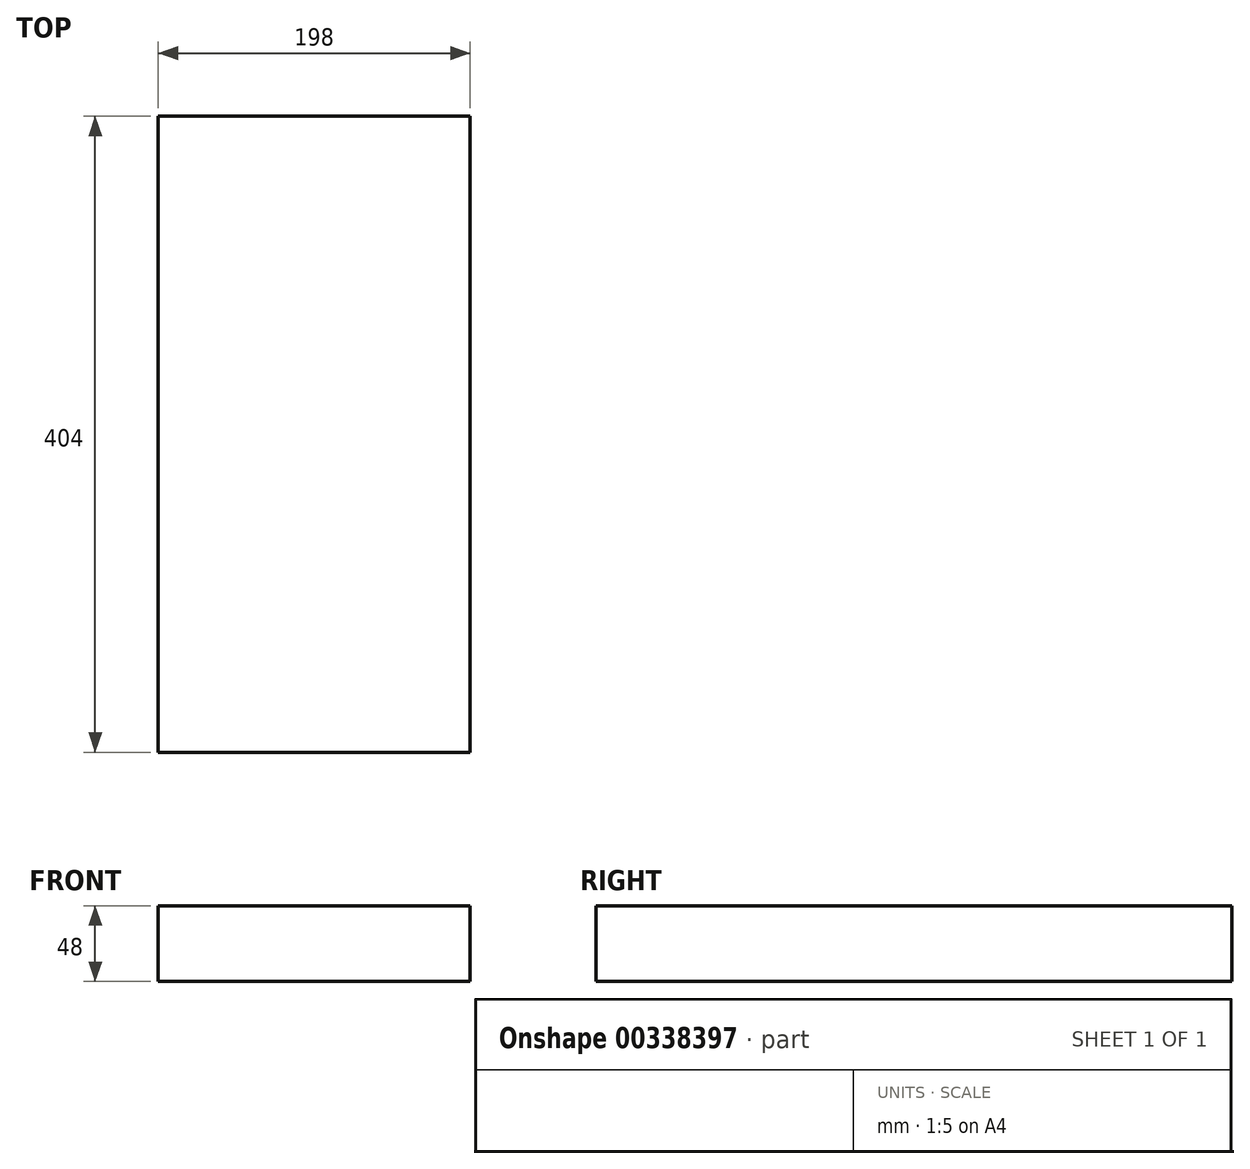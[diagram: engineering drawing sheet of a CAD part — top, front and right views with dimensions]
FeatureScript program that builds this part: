
annotation { "Feature Type Name" : "Feature", "Feature Type Description" : "" }
export const myFeature = defineFeature(function(context is Context, id is Id, definition is map)
    precondition{}
    {
        {
            var Q0;
            Q0=qCreatedBy(makeId("Front.planeOp"),FACE);
            var sketch = newSketch(context, id + "F0", { "sketchPlane" : qUnion([Q0])});
            skLineSegment(sketch, "E0.bottom", {"start": v(-99, -24) * mm, "end": v(99, -24) * mm});
            skLineSegment(sketch, "E0.top", {"start": v(-99, 24) * mm, "end": v(99, 24) * mm});
            skLineSegment(sketch, "E0.left", {"start": v(-99, -24) * mm, "end": v(-99, 24) * mm});
            skLineSegment(sketch, "E0.right", {"start": v(99, -24) * mm, "end": v(99, 24) * mm});
            skPoint(sketch, "E0.middle", {"position": v(0, 0) * mm});
            skSolve(sketch);
        }
        {
            var Q0;
            Q0=makeQuery(id+"F0.imprint","IMPRINT",FACE,{"disambiguationData":[TD([[makeQuery(id+"F0.imprint","IMPRINT",EDGE,{"derivedFrom":sQuery(id+"F0.wireOp",EDGE,"E0.bottom")}),1.0]])]});
            extrude(context, id + "F1", {"entities" : qUnion([Q0]), "offsetDistance" : 25 * mm, "depth" : 404 * mm});
        }
    });
